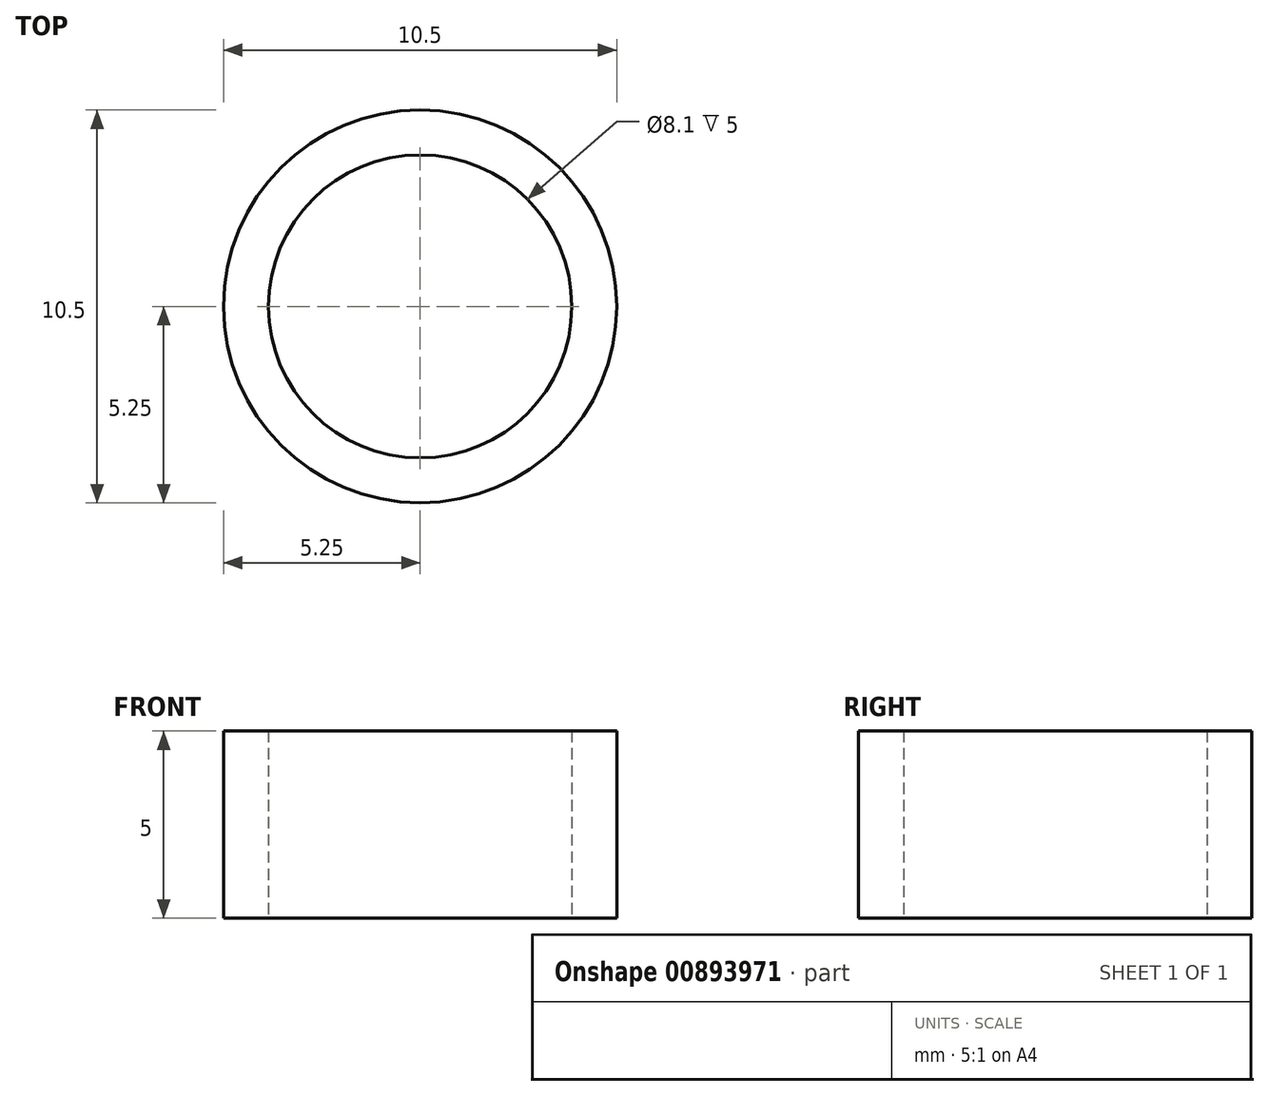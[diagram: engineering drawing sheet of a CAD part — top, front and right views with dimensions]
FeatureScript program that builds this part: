
annotation { "Feature Type Name" : "Feature", "Feature Type Description" : "" }
export const myFeature = defineFeature(function(context is Context, id is Id, definition is map)
    precondition{}
    {
        {
            var Q0;
            Q0=qCreatedBy(makeId("Top.planeOp"),FACE);
            var sketch = newSketch(context, id + "F0", { "sketchPlane" : qUnion([Q0])});
            skCircle(sketch, "E0", {"center": v(0, 0) * mm, "radius": 4.05 * mm});
            skCircle(sketch, "E1", {"center": v(0, 0) * mm, "radius": 5.25 * mm});
            skSolve(sketch);
        }
        {
            var Q0;
            Q0 = qSketchRegion(id + "F0", true);
            extrude(context, id + "F1", {"entities" : qUnion([Q0]), "depth" : 5 * mm, "offsetDistance" : 25 * mm});
        }
    });
